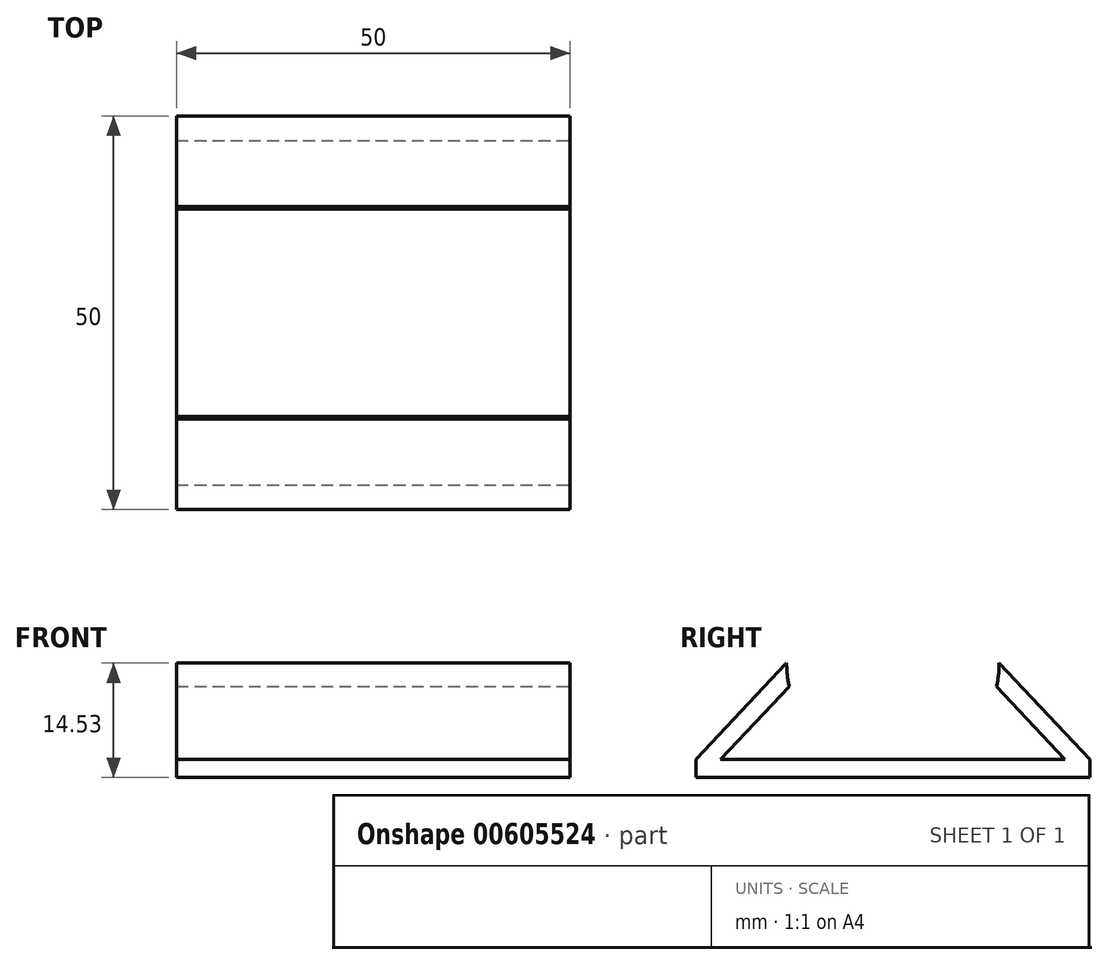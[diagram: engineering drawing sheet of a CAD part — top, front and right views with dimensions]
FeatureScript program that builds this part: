
annotation { "Feature Type Name" : "Feature", "Feature Type Description" : "" }
export const myFeature = defineFeature(function(context is Context, id is Id, definition is map)
    precondition{}
    {
        {
            var Q0;
            Q0=qCreatedBy(makeId("Top.planeOp"),FACE);
            var sketch = newSketch(context, id + "F0", { "sketchPlane" : qUnion([Q0])});
            skLineSegment(sketch, "E0.bottom", {"start": v(25, -25) * mm, "end": v(-25, -25) * mm});
            skLineSegment(sketch, "E0.top", {"start": v(25, 25) * mm, "end": v(-25, 25) * mm});
            skLineSegment(sketch, "E0.left", {"start": v(25, -25) * mm, "end": v(25, 25) * mm});
            skLineSegment(sketch, "E0.right", {"start": v(-25, -25) * mm, "end": v(-25, 25) * mm});
            skPoint(sketch, "E0.middle", {"position": v(0, 0) * mm});
            skSolve(sketch);
        }
        {
            var Q0;
            Q0=makeQuery(id+"F0.imprint","IMPRINT",FACE,{"disambiguationData":[TD([[makeQuery(id+"F0.imprint","IMPRINT",EDGE,{"derivedFrom":sQuery(id+"F0.wireOp",EDGE,"E0.bottom")}),-1.0]])]});
            extrude(context, id + "F1", {"entities" : qUnion([Q0]), "depth" : 2.28 * mm, "offsetDistance" : 25 * mm});
        }
        {
            var Q0;
            Q0=makeQuery(id+"F1.opExtrude","SWEPT_FACE",FACE,{"disambiguationData":[OSD([sQuery(id+"F0.wireOp",EDGE,"E0.left")])]});
            var sketch = newSketch(context, id + "F2", { "sketchPlane" : qUnion([Q0])});
            skLineSegment(sketch, "E1", {"start": v(-25, 2.28) * mm, "end": v(-25, 14.53) * mm});
            skLineSegment(sketch, "E2", {"start": v(-25, 14.53) * mm, "end": v(25, 14.53) * mm});
            skLineSegment(sketch, "E3", {"start": v(25, 14.53) * mm, "end": v(25, 2.28) * mm});
            skCircle(sketch, "E4", {"center": v(0, 14.53) * mm, "radius": 13.5 * mm});
            skLineSegment(sketch, "E5", {"start": v(-13.5, 14.53) * mm, "end": v(-25, 2.28) * mm});
            skLineSegment(sketch, "E6", {"start": v(-21.87, 2.28) * mm, "end": v(-13.17, 11.55) * mm});
            skLineSegment(sketch, "E7", {"start": v(13.5, 14.53) * mm, "end": v(25, 2.28) * mm});
            skLineSegment(sketch, "E8", {"start": v(21.87, 2.28) * mm, "end": v(13.17, 11.55) * mm});
            skLineSegment(sketch, "E9", {"start": v(-13.5, 14.53) * mm, "end": v(-13.17, 11.55) * mm});
            skLineSegment(sketch, "E10", {"start": v(13.17, 11.55) * mm, "end": v(13.5, 14.53) * mm});
            skSolve(sketch);
        }
        {
            var Q0;
            {var subQ1=sQuery(id+"F2.wireOp",EDGE,"E5");Q0=makeQuery(id+"F2.imprint","IMPRINT",FACE,{"disambiguationData":[TD([[makeQuery(id+"F2.imprint","IMPRINT",EDGE,{"derivedFrom":subQ1}),1.0]])]});}
            var Q1;
            {var subQ1=sQuery(id+"F2.wireOp",EDGE,"E7");Q1=makeQuery(id+"F2.imprint","IMPRINT",FACE,{"disambiguationData":[TD([[makeQuery(id+"F2.imprint","IMPRINT",EDGE,{"derivedFrom":subQ1}),-1.0]])]});}
            extrude(context, id + "F3", {"entities" : qUnion([Q0, Q1]), "operationType" : NewBodyOperationType.ADD, "oppositeDirection" : true, "depth" : 50 * mm, "offsetDistance" : 25 * mm});
        }
    });
